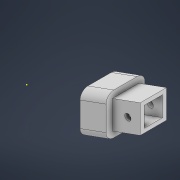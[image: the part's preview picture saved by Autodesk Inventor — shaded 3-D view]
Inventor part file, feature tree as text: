
AUTODESK INVENTOR PART (.ipt)
format: ipt  version: 2021 (Build 250183000, 183)  size: 372,224 bytes
history: native  units: mm
features: extrude x11, sketch x8, other x1, shell x1, fillet x1
ambient origin geometry x8: Origin, YZ Plane, XZ Plane, XY Plane, X Axis, Y Axis, Z Axis, Center Point
bodies: Body1 (feature_tree)
feature tree (22):
  other  "Servohalterung_v2"
  extrude  "Extrusion2"  Depth=20.2mm
  extrude  "Extrusion3"  Depth=7.0mm
  sketch  "Skizze3"  dims[d9=4.0mm d10=0.0mm d11=3.2mm]
  extrude  "Extrusion4"  Depth=4.0mm
  extrude  "Extrusion5"  Depth=10.0mm
  extrude  "Extrusion6"  Depth=4.0mm TaperAngle=0.0deg
  sketch  "Skizze6"  dims[d12=3.2mm d15=10.0mm]
  extrude  "Extrusion7"  Depth=1.5mm
  extrude  "Extrusion9"  Depth=2.0mm
  shell  "Wandung2"  Thickness=2.0mm
  fillet  "Rundung1"  Radius=3.0mm
  extrude  "Extrusion10"  Depth=20.0mm
  extrude  "Extrusion11"  Depth=10.0mm
  extrude  "Extrusion12"  Depth=10.0mm
  extrude  "Extrusion13"  Depth=10.0mm TaperAngle=0.0deg
  sketch  "Skizze1"  dims[d0=41.0mm d3=20.2mm]
  sketch  "Skizze2"  dims[d7=58.0mm d8=7.0mm]
  sketch  "Skizze7"  dims[d16=5.0mm d17=4.0mm d18=0.0mm]
  sketch  "Skizze8"  dims[d19=7.0mm d20=1.5mm]
  sketch  "Skizze9"  dims[d21=2.0mm d22=0.0mm d23=7.0mm d24=2.0mm d25=0.0mm d26=3.0mm]
  sketch  "Skizze10"  dims[d27=21.216mm d28=20.0mm d29=21.216mm d30=3.490659mm d31=34.2mm d32=0.0mm d33=20.0mm d34=0.0mm d36=4.0mm d38=19.198622mm d42=18.0mm d44=19.198622mm d48=14.314467mm d51=13.5mm d52=0.0mm d53=2.0mm d54=2.0mm d55=0.0mm d56=2.0mm d57=0.0mm d58=3.5mm d59=3.5mm d60=3.2mm d62=27.925268mm d63=8.0mm d64=10.0mm d65=0.0mm d66=14.5mm d67=27.925268mm d68=50.0mm d69=0.0mm]
